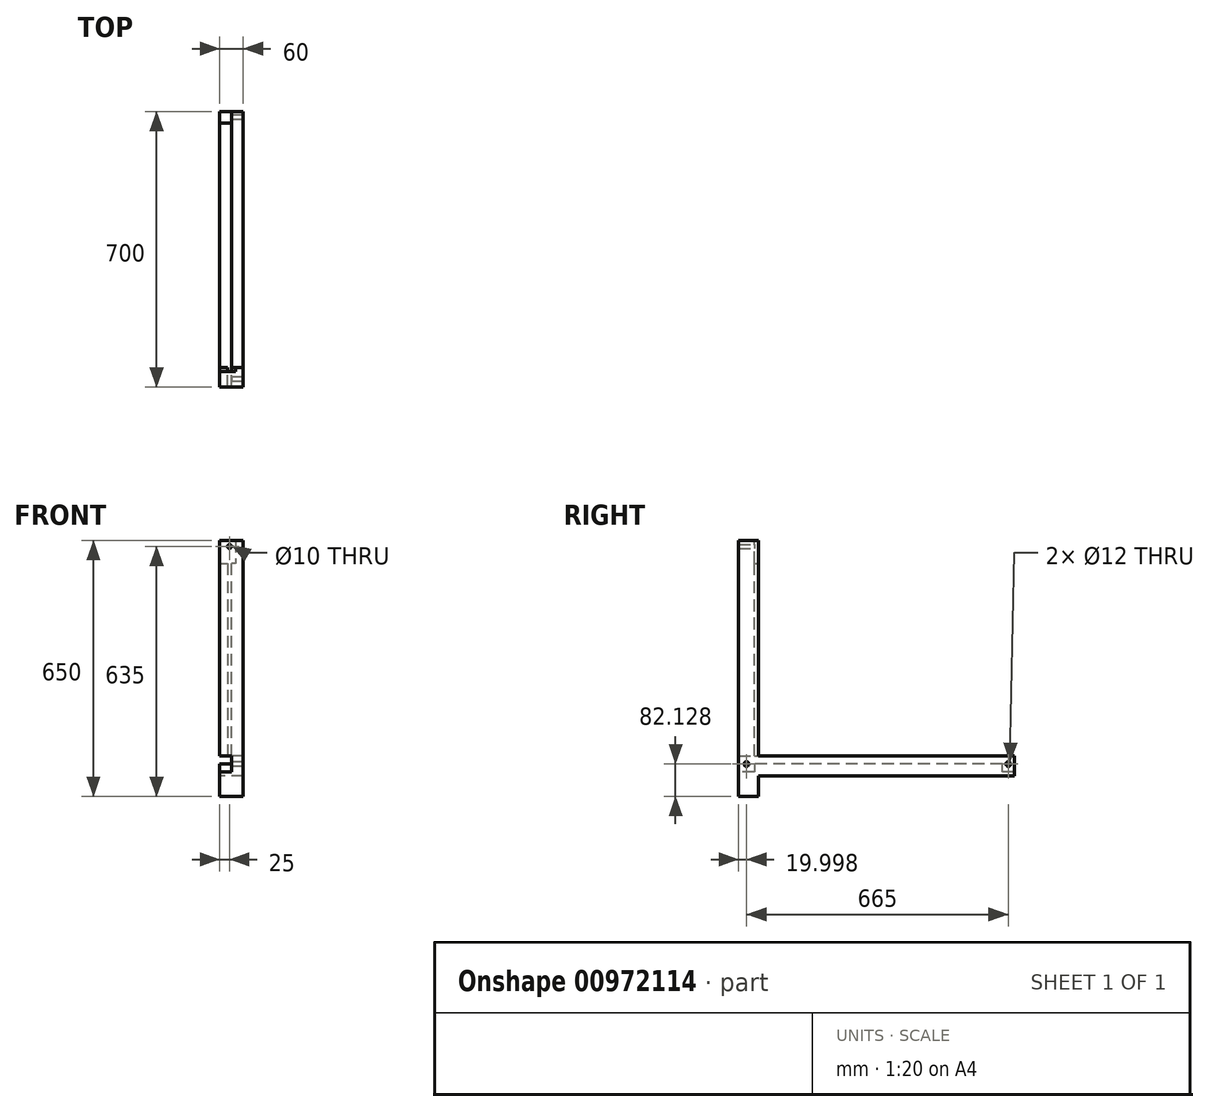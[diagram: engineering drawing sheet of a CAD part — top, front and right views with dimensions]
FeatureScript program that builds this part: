
annotation { "Feature Type Name" : "Feature", "Feature Type Description" : "" }
export const myFeature = defineFeature(function(context is Context, id is Id, definition is map)
    precondition{}
    {
        {
            var Q0;
            Q0=qCreatedBy(makeId("Right.planeOp"),FACE);
            var sketch = newSketch(context, id + "F0", { "sketchPlane" : qUnion([Q0])});
            skLineSegment(sketch, "E0", {"start": v(-346.18, 422.54) * mm, "end": v(-346.18, -227.46) * mm});
            skLineSegment(sketch, "E1", {"start": v(-346.18, -227.46) * mm, "end": v(-296.18, -227.46) * mm});
            skLineSegment(sketch, "E2", {"start": v(-296.18, -227.46) * mm, "end": v(-296.18, -175.33) * mm});
            skLineSegment(sketch, "E3", {"start": v(-296.18, -175.33) * mm, "end": v(353.82, -175.33) * mm});
            skLineSegment(sketch, "E4", {"start": v(353.82, -175.33) * mm, "end": v(353.82, -125.33) * mm});
            skLineSegment(sketch, "E5", {"start": v(353.82, -125.33) * mm, "end": v(-296.18, -125.33) * mm});
            skLineSegment(sketch, "E6", {"start": v(-296.18, -125.33) * mm, "end": v(-296.18, 422.54) * mm});
            skLineSegment(sketch, "E7", {"start": v(-296.18, 422.54) * mm, "end": v(-346.18, 422.54) * mm});
            skSolve(sketch);
        }
        {
            var Q0;
            Q0 = qSketchRegion(id + "F0", true);
            extrude(context, id + "F1", {"entities" : qUnion([Q0]), "depth" : 60 * mm, "offsetDistance" : 25 * mm});
        }
        {
            var Q0;
            Q0=makeQuery(id+"F1.opExtrude","CAP_FACE",FACE,{"disambiguationData":[OSD([sQuery(id+"F0.wireOp",EDGE,"E0"),sQuery(id+"F0.wireOp",EDGE,"E1"),sQuery(id+"F0.wireOp",EDGE,"E2"),sQuery(id+"F0.wireOp",EDGE,"E3"),sQuery(id+"F0.wireOp",EDGE,"E4"),sQuery(id+"F0.wireOp",EDGE,"E5"),sQuery(id+"F0.wireOp",EDGE,"E6"),sQuery(id+"F0.wireOp",EDGE,"E7")])],"isStart":true});
            var sketch = newSketch(context, id + "F2", { "sketchPlane" : qUnion([Q0])});
            skLineSegment(sketch, "E8", {"start": v(-353.82, -125.33) * mm, "end": v(-353.82, -165.33) * mm});
            skLineSegment(sketch, "E9", {"start": v(-353.82, -165.33) * mm, "end": v(-323.82, -165.33) * mm});
            skLineSegment(sketch, "E10", {"start": v(-323.82, -165.33) * mm, "end": v(-323.82, -145.33) * mm});
            skLineSegment(sketch, "E11", {"start": v(-323.82, -145.33) * mm, "end": v(306.18, -145.33) * mm});
            skLineSegment(sketch, "E12", {"start": v(306.18, -145.33) * mm, "end": v(306.18, -165.33) * mm});
            skLineSegment(sketch, "E13", {"start": v(306.18, -165.33) * mm, "end": v(346.18, -165.33) * mm});
            skLineSegment(sketch, "E14", {"start": v(346.18, -165.33) * mm, "end": v(346.18, -125.33) * mm});
            skLineSegment(sketch, "E15", {"start": v(346.18, -125.33) * mm, "end": v(-353.82, -125.33) * mm});
            skSolve(sketch);
        }
        {
            var Q0;
            Q0 = qSketchRegion(id + "F2", true);
            extrude(context, id + "F3", {"entities" : qUnion([Q0]), "operationType" : NewBodyOperationType.REMOVE, "oppositeDirection" : true, "depth" : 30 * mm, "offsetDistance" : 25 * mm});
        }
        {
            var Q0;
            Q0=makeQuery(id+"F3.boolean.opBoolean","COPY",FACE,{"derivedFrom":makeQuery(id+"F3.opExtrude","CAP_FACE",FACE,{"disambiguationData":[OSD([sQuery(id+"F2.wireOp",EDGE,"E8"),sQuery(id+"F2.wireOp",EDGE,"E9"),sQuery(id+"F2.wireOp",EDGE,"E10"),sQuery(id+"F2.wireOp",EDGE,"E11"),sQuery(id+"F2.wireOp",EDGE,"E12"),sQuery(id+"F2.wireOp",EDGE,"E13"),sQuery(id+"F2.wireOp",EDGE,"E14"),sQuery(id+"F2.wireOp",EDGE,"E15")])],"isStart":false})});
            var sketch = newSketch(context, id + "F4", { "sketchPlane" : qUnion([Q0])});
            skPoint(sketch, "E16", {"position": v(326.18, -145.33) * mm});
            skPoint(sketch, "E16.positionSnap0", {"position": v(326.18, -165.33) * mm});
            skPoint(sketch, "E17", {"position": v(-338.82, -145.33) * mm});
            skPoint(sketch, "E17.positionSnap0", {"position": v(-353.82, -145.33) * mm});
            skPoint(sketch, "E17.positionSnap1", {"position": v(-338.82, -165.33) * mm});
            skSolve(sketch);
        }
        {
            var Q0;
            Q0=sQuery(id+"F4.wireOp",VERTEX,"E17");
            var Q1;
            Q1=sQuery(id+"F4.wireOp",VERTEX,"E16");
            var Q2;
            Q2=makeQuery(id+"F1.opExtrude","SWEPT_BODY",BODY,{"disambiguationData":[OSD([sQuery(id+"F0.wireOp",EDGE,"E0"),sQuery(id+"F0.wireOp",EDGE,"E1"),sQuery(id+"F0.wireOp",EDGE,"E2"),sQuery(id+"F0.wireOp",EDGE,"E3"),sQuery(id+"F0.wireOp",EDGE,"E4"),sQuery(id+"F0.wireOp",EDGE,"E5"),sQuery(id+"F0.wireOp",EDGE,"E6"),sQuery(id+"F0.wireOp",EDGE,"E7")])]});
            hole(context, id + "F5", {"style" : HoleStyle.SIMPLE, "endStyle" : HoleEndStyle.THROUGH, "holeDiameter" : 12 * mm, "majorDiameter" : 5 * mm, "isTappedThrough" : true, "tappedDepth" : 12 * mm, "tapClearance" : 3, "locations" : qUnion([Q0, Q1]), "scope" : qUnion([Q2])});
        }
        {
            var Q0;
            Q0=makeQuery(id+"F3.boolean.opBoolean","MERGE",FACE,{"derivedFrom":[makeQuery(id+"F1.opExtrude","SWEPT_FACE",FACE,{"disambiguationData":[OSD([sQuery(id+"F0.wireOp",EDGE,"E6")])]})],"fromTools":[makeQuery(id+"F3.opExtrude","SWEPT_FACE",FACE,{"disambiguationData":[OSD([sQuery(id+"F2.wireOp",EDGE,"E14")])]})]});
            var sketch = newSketch(context, id + "F6", { "sketchPlane" : qUnion([Q0])});
            skLineSegment(sketch, "E18", {"start": v(-30, -125.33) * mm, "end": v(-30, 364.67) * mm});
            skLineSegment(sketch, "E19", {"start": v(0, 374.67) * mm, "end": v(0, 364.67) * mm});
            skLineSegment(sketch, "E20", {"start": v(0, 364.67) * mm, "end": v(-20, 364.67) * mm});
            skLineSegment(sketch, "E21", {"start": v(-20, 364.67) * mm, "end": v(-20, -125.33) * mm});
            skLineSegment(sketch, "E22", {"start": v(-20, -125.33) * mm, "end": v(-30, -125.33) * mm});
            skPoint(sketch, "E23.endSnap0", {"position": v(-30, 422.54) * mm});
            skLineSegment(sketch, "E24", {"start": v(-40, 422.54) * mm, "end": v(0, 422.54) * mm});
            skLineSegment(sketch, "E25", {"start": v(0, 422.54) * mm, "end": v(0, 374.67) * mm});
            skLineSegment(sketch, "E26", {"start": v(-40, 422.54) * mm, "end": v(-40, 364.67) * mm});
            skLineSegment(sketch, "E27", {"start": v(-40, 364.67) * mm, "end": v(-30, 364.67) * mm});
            skSolve(sketch);
        }
        {
            var Q0;
            Q0 = qSketchRegion(id + "F6", true);
            extrude(context, id + "F7", {"entities" : qUnion([Q0]), "operationType" : NewBodyOperationType.REMOVE, "oppositeDirection" : true, "depth" : 10 * mm, "offsetDistance" : 25 * mm});
        }
        {
            var Q0;
            Q0=makeQuery(id+"F7.boolean.opBoolean","COPY",FACE,{"derivedFrom":makeQuery(id+"F7.opExtrude","CAP_FACE",FACE,{"disambiguationData":[OSD([sQuery(id+"F6.wireOp",EDGE,"E18"),sQuery(id+"F6.wireOp",EDGE,"E19"),sQuery(id+"F6.wireOp",EDGE,"E20"),sQuery(id+"F6.wireOp",EDGE,"E21"),sQuery(id+"F6.wireOp",EDGE,"E22"),sQuery(id+"F6.wireOp",EDGE,"E24"),sQuery(id+"F6.wireOp",EDGE,"E25"),sQuery(id+"F6.wireOp",EDGE,"E26"),sQuery(id+"F6.wireOp",EDGE,"E27")])],"isStart":false})});
            var sketch = newSketch(context, id + "F8", { "sketchPlane" : qUnion([Q0])});
            skPoint(sketch, "E28", {"position": v(-25, 407.54) * mm});
            skSolve(sketch);
        }
        {
            var Q0;
            Q0=sQuery(id+"F8.wireOp",VERTEX,"E28");
            var Q1;
            Q1=makeQuery(id+"F1.opExtrude","SWEPT_BODY",BODY,{"disambiguationData":[OSD([sQuery(id+"F0.wireOp",EDGE,"E0"),sQuery(id+"F0.wireOp",EDGE,"E1"),sQuery(id+"F0.wireOp",EDGE,"E2"),sQuery(id+"F0.wireOp",EDGE,"E3"),sQuery(id+"F0.wireOp",EDGE,"E4"),sQuery(id+"F0.wireOp",EDGE,"E5"),sQuery(id+"F0.wireOp",EDGE,"E6"),sQuery(id+"F0.wireOp",EDGE,"E7")])]});
            hole(context, id + "F9", {"style" : HoleStyle.SIMPLE, "endStyle" : HoleEndStyle.THROUGH, "holeDiameter" : 10 * mm, "majorDiameter" : 5 * mm, "isTappedThrough" : true, "tappedDepth" : 12 * mm, "tapClearance" : 3, "locations" : qUnion([Q0]), "scope" : qUnion([Q1])});
        }
    });
